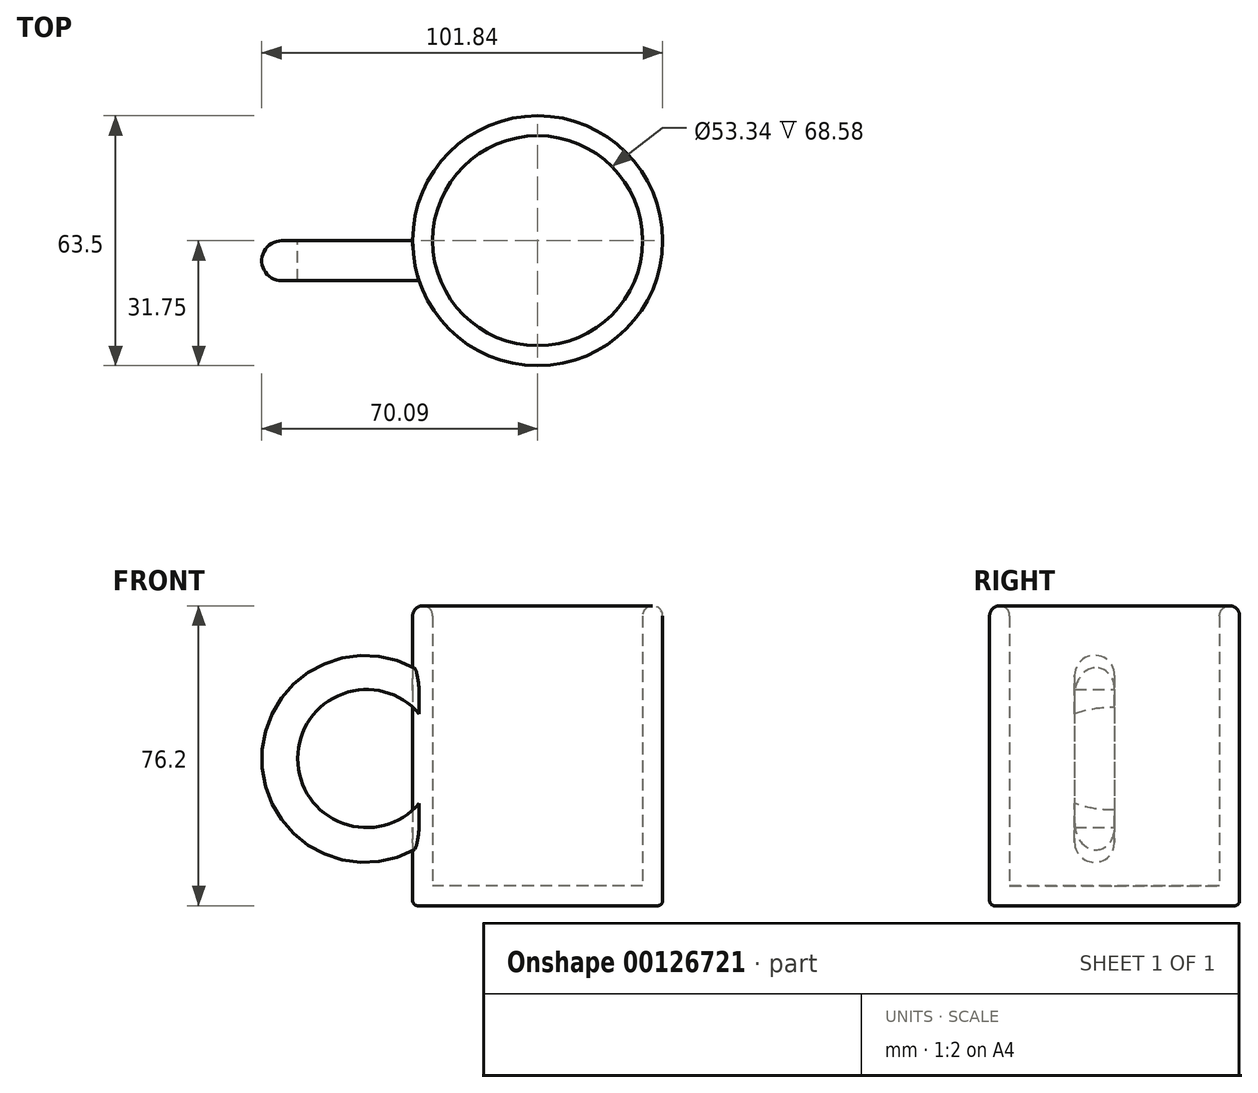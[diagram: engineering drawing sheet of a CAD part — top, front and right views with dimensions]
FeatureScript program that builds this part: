
annotation { "Feature Type Name" : "Feature", "Feature Type Description" : "" }
export const myFeature = defineFeature(function(context is Context, id is Id, definition is map)
    precondition{}
    {
        {
            var Q0;
            Q0=qCreatedBy(makeId("Top.planeOp"),FACE);
            var sketch = newSketch(context, id + "F0", { "sketchPlane" : qUnion([Q0])});
            skCircle(sketch, "E0", {"center": v(0, 0) * mm, "radius": 31.75 * mm});
            skSolve(sketch);
        }
        {
            var Q0;
            Q0 = qSketchRegion(id + "F0", true);
            extrude(context, id + "F1", {"entities" : qUnion([Q0]), "depth" : 76.2 * mm});
        }
        {
            var Q0;
            Q0=makeQuery(id+"F1.opExtrude","CAP_FACE",FACE,{"disambiguationData":[OSD([sQuery(id+"F0.wireOp",EDGE,"E0")])],"isStart":false});
            shell(context, id + "F2", {"entities" : qUnion([Q0]), "thickness" : 5.08 * mm});
        }
        {
            var Q0;
            Q0=makeQuery(id+"F1.opExtrude","CAP_FACE",FACE,{"disambiguationData":[OSD([sQuery(id+"F0.wireOp",EDGE,"E0")])],"isStart":false});
            fillet(context, id + "F3", {"entities" : qUnion([Q0]), "radius" : 2.54 * mm, "tangentPropagation" : true, "allowEdgeOverflow" : false});
        }
        {
            var Q0;
            Q0=makeQuery(id+"F1.opExtrude","CAP_FACE",FACE,{"disambiguationData":[OSD([sQuery(id+"F0.wireOp",EDGE,"E0")])],"isStart":true});
            fillet(context, id + "F4", {"entities" : qUnion([Q0]), "radius" : 1.27 * mm, "tangentPropagation" : true, "allowEdgeOverflow" : false});
        }
        {
            var Q0;
            Q0=qCreatedBy(makeId("Front.planeOp"),FACE);
            var sketch = newSketch(context, id + "F5", { "sketchPlane" : qUnion([Q0])});
            skArc(sketch, "E1", {"start": v(-28.46, 58.65) * mm, "mid": v(-70.1, 37.03) * mm, "end": v(-28, 16.34) * mm});
            skArc(sketch, "E2", {"start": v(-29.33, 47.85) * mm, "mid": v(-60.93, 36.15) * mm, "end": v(-28, 29.03) * mm});
            skLineSegment(sketch, "E3", {"start": v(-28.46, 58.65) * mm, "end": v(-29.33, 47.85) * mm});
            skLineSegment(sketch, "E4", {"start": v(-28, 29.03) * mm, "end": v(-28, 16.34) * mm});
            skSolve(sketch);
        }
        {
            var Q0;
            Q0 = qSketchRegion(id + "F5", true);
            extrude(context, id + "F6", {"entities" : qUnion([Q0]), "operationType" : NewBodyOperationType.ADD, "depth" : 10.16 * mm});
        }
        {
            var Q0;
            Q0=makeQuery(id+"F6.opExtrude","CAP_EDGE",EDGE,{"disambiguationData":[OSD([sQuery(id+"F5.wireOp",EDGE,"E1")])],"isStart":false});
            var Q1;
            Q1=makeQuery(id+"F6.opExtrude","CAP_EDGE",EDGE,{"disambiguationData":[OSD([sQuery(id+"F5.wireOp",EDGE,"E1")])],"isStart":true});
            fillet(context, id + "F7", {"entities" : qUnion([Q0, Q1]), "radius" : 5.08 * mm, "tangentPropagation" : true, "allowEdgeOverflow" : false});
        }
    });
